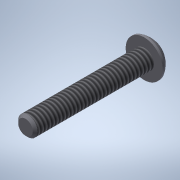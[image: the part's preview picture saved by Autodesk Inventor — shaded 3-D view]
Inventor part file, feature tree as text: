
AUTODESK INVENTOR PART (.ipt)
format: ipt  version: 2020 (Build 240168000, 168)  size: 134,144 bytes
history: native  units: in
note: dims shown in document units (in); Inventor stores cm internally (conversion verified against a paired STEP export)
features: sketch x3, extrude x2, revolve x1, chamfer x1, thread x1
ambient origin geometry x8: Origin, YZ Plane, XZ Plane, XY Plane, X Axis, Y Axis, Z Axis, Center Point
bodies: Solid1 (feature_tree)
feature tree (8):
  extrude  "Extrusion1"  Depth=1.0in TaperAngle=0.0deg
  revolve  "Revolution1"  [1 undecoded]
  extrude  "Extrusion2"  Depth=0.0938in
  chamfer  "Chamfer1"  Distance=0.0625in
  thread  "Thread1"  [1 undecoded]
  sketch  "Sketch1"  dims[d0=0.164in d1=1.0in d2=0.0in]
  sketch  "Sketch2"  dims[d3=0.087in d6=0.08in]
  sketch  "Sketch3"  dims[d7=90.0deg d8=0.0938in d9=0.0625in d10=0.0in d13=0.02in d14=0.125in d15=45.0deg d16=1.0in d17=0.0in d19=0.156in]
note: 2 required parameter values undecoded (feature->parameter linkage not recoverable at this tier; creation-order binding heuristic only, values carry confidence <= 0.55)